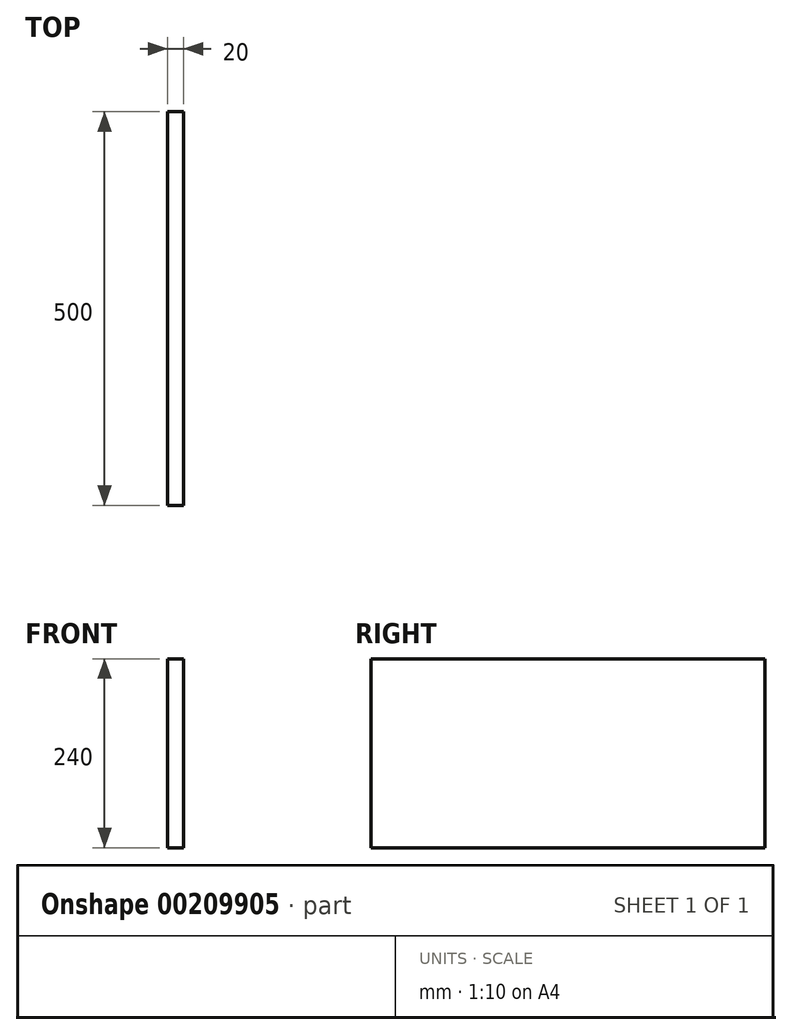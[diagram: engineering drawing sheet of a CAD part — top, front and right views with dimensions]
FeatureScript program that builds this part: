
annotation { "Feature Type Name" : "Feature", "Feature Type Description" : "" }
export const myFeature = defineFeature(function(context is Context, id is Id, definition is map)
    precondition{}
    {
        {
            var Q0;
            Q0=qCreatedBy(makeId("Right.planeOp"),FACE);
            var sketch = newSketch(context, id + "F0", { "sketchPlane" : qUnion([Q0])});
            skLineSegment(sketch, "E0.bottom", {"start": v(-250, 120) * mm, "end": v(250, 120) * mm});
            skLineSegment(sketch, "E0.top", {"start": v(-250, -120) * mm, "end": v(250, -120) * mm});
            skLineSegment(sketch, "E0.left", {"start": v(-250, 120) * mm, "end": v(-250, -120) * mm});
            skLineSegment(sketch, "E0.right", {"start": v(250, 120) * mm, "end": v(250, -120) * mm});
            skPoint(sketch, "E0.middle", {"position": v(0, 0) * mm});
            skSolve(sketch);
        }
        {
            var Q0;
            Q0=makeQuery(id+"F0.imprint","IMPRINT",FACE,{"disambiguationData":[TD([[makeQuery(id+"F0.imprint","IMPRINT",EDGE,{"derivedFrom":sQuery(id+"F0.wireOp",EDGE,"E0.bottom")}),-1.0]])]});
            extrude(context, id + "F1", {"entities" : qUnion([Q0]), "depth" : 20 * mm});
        }
    });
